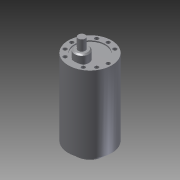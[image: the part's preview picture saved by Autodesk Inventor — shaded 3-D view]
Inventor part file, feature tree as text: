
AUTODESK INVENTOR PART (.ipt)
format: ipt  version: 2012 (Build 160160000, 160)  size: 137,728 bytes
history: native  units: mm
features: extrude x6, sketch x2, chamfer x1
ambient origin geometry x8: Origin, YZ Plane, XZ Plane, XY Plane, X Axis, Y Axis, Z Axis, Center Point
bodies: Solid1 (feature_tree)
feature tree (9):
  sketch  "Sketch1"  dims[d0=36.8mm d1=6.0mm]
  extrude  "Extrusion1"  Depth=6.0mm
  extrude  "Extrusion2"  Depth=64.516mm TaperAngle=0.0deg
  extrude  "Extrusion3"  Depth=6.5mm TaperAngle=0.0deg
  extrude  "Extrusion4"  Depth=15.5mm TaperAngle=0.0deg
  chamfer  "Chamfer1"  Distance=24.1mm
  extrude  "Extrusion5"  Depth=5.6mm TaperAngle=0.0deg
  extrude  "Extrusion6"  Depth=1.0mm TaperAngle=45.0deg
  sketch  "Sketch2"  dims[d3=12.0mm d4=64.516mm d5=0.0mm d6=6.5mm d7=0.0mm d8=15.5mm d9=0.0mm d10=24.1mm d11=5.6mm d12=0.0mm d13=1.0mm d14=2.0mm d15=45.0deg d16=3.2mm d17=15.5mm d19=8.02339mm d20=8.02339mm d21=8.02339mm d22=8.02339mm d25=31.0mm d26=31.0mm d27=31.0mm d28=15.5mm d29=15.5mm d30=8.02339mm d31=8.02339mm d32=7.0mm d33=1.0mm d34=0.0mm d35=10.0mm d36=0.0mm]
